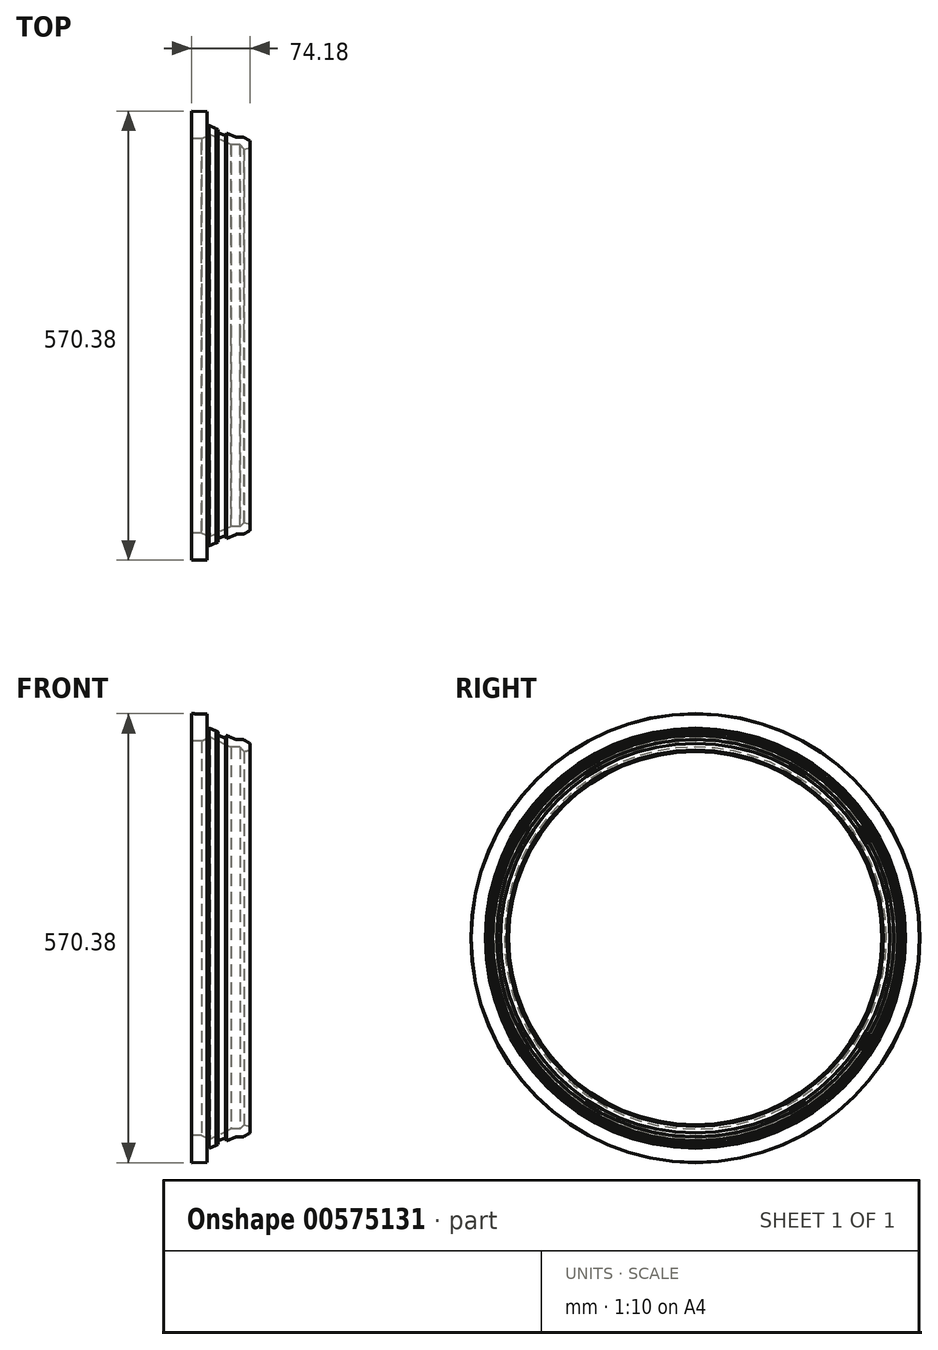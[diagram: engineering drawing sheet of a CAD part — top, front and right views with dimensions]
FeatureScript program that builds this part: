
annotation { "Feature Type Name" : "Feature", "Feature Type Description" : "" }
export const myFeature = defineFeature(function(context is Context, id is Id, definition is map)
    precondition{}
    {
        {
            var Q0;
            Q0=qCreatedBy(makeId("Front.planeOp"),FACE);
            var sketch = newSketch(context, id + "F0", { "sketchPlane" : qUnion([Q0])});
            skLineSegment(sketch, "E0", {"start": v(0, 0) * mm, "end": v(30.12, 0) * mm});
            skPoint(sketch, "E1", {"position": v(-7.36, 231.93) * mm});
            skLineSegment(sketch, "E2", {"start": v(-7.36, 237.1) * mm, "end": v(0, 239.08) * mm});
            skLineSegment(sketch, "E3.trimOffspring", {"start": v(0, 239.08) * mm, "end": v(0, 245.2) * mm});
            skLineSegment(sketch, "E4", {"start": v(-7.36, 237.1) * mm, "end": v(-12.82, 242.57) * mm});
            skLineSegment(sketch, "E5", {"start": v(-16.97, 252.22) * mm, "end": v(-8.98, 252.22) * mm});
            skLineSegment(sketch, "E6", {"start": v(-97.44, 148.32) * mm, "end": v(22.45, 148.32) * mm});
            skLineSegment(sketch, "E7", {"start": v(-97.44, 193.92) * mm, "end": v(-97.44, 70.08) * mm});
            skPoint(sketch, "E8", {"position": v(-66.59, 139.32) * mm});
            skArc(sketch, "E9", {"start": v(0, 247.47) * mm, "mid": v(-3.92, 249.79) * mm, "end": v(-7.93, 251.96) * mm});
            skLineSegment(sketch, "E10", {"start": v(0, 0) * mm, "end": v(0, 148.32) * mm});
            skArc(sketch, "E11.trimOffspring", {"start": v(-43.28, 263.2) * mm, "mid": v(-47.44, 265.06) * mm, "end": v(-51.66, 266.78) * mm});
            skLineSegment(sketch, "E12", {"start": v(-43.28, 263.2) * mm, "end": v(-40.28, 261.92) * mm});
            skLineSegment(sketch, "E13", {"start": v(-40.28, 261.92) * mm, "end": v(-41.77, 258.41) * mm});
            skLineSegment(sketch, "E14", {"start": v(-41.77, 258.41) * mm, "end": v(-31.25, 253.95) * mm});
            skLineSegment(sketch, "E15", {"start": v(-31.25, 253.95) * mm, "end": v(-29.76, 257.46) * mm});
            skLineSegment(sketch, "E16.trimOffspring", {"start": v(-29.76, 257.46) * mm, "end": v(-17.86, 252.4) * mm});
            skLineSegment(sketch, "E17.trimOffspring", {"start": v(0, 240.83) * mm, "end": v(0, 246.18) * mm});
            skLineSegment(sketch, "E18", {"start": v(-51.66, 266.78) * mm, "end": v(-52.3, 266.15) * mm});
            skLineSegment(sketch, "E19", {"start": v(-54.33, 266.06) * mm, "end": v(-52.5, 266.06) * mm});
            skLineSegment(sketch, "E20", {"start": v(-54.61, 284.8) * mm, "end": v(-54.61, 266.35) * mm});
            skLineSegment(sketch, "E21", {"start": v(-24.13, 242.57) * mm, "end": v(-13.94, 242.57) * mm});
            skPoint(sketch, "E22", {"position": v(-24.13, 242.57) * mm});
            skLineSegment(sketch, "E23", {"start": v(-13.94, 242.57) * mm, "end": v(-12.82, 242.57) * mm});
            skLineSegment(sketch, "E24", {"start": v(-24.13, 242.57) * mm, "end": v(-50.68, 255.32) * mm});
            skLineSegment(sketch, "E25", {"start": v(-50.68, 255.32) * mm, "end": v(-61.45, 250.42) * mm});
            skLineSegment(sketch, "E26", {"start": v(-61.45, 250.42) * mm, "end": v(-74.18, 250.42) * mm});
            skLineSegment(sketch, "E27", {"start": v(-74.18, 250.42) * mm, "end": v(-74.18, 285.19) * mm});
            skLineSegment(sketch, "E28", {"start": v(-74.18, 285.19) * mm, "end": v(-54.61, 284.8) * mm});
            skPoint(sketch, "E29.visualSharp", {"position": v(0, 247.47) * mm});
            skPoint(sketch, "E30.visualSharp", {"position": v(0, 239.08) * mm});
            skPoint(sketch, "E31.visualSharp", {"position": v(-8.43, 252.22) * mm});
            skArc(sketch, "E31.filletArc", {"start": v(-7.93, 251.96) * mm, "mid": v(-8.44, 252.16) * mm, "end": v(-8.98, 252.22) * mm});
            skPoint(sketch, "E32.visualSharp", {"position": v(-17.43, 252.22) * mm});
            skArc(sketch, "E32.filletArc", {"start": v(-17.86, 252.4) * mm, "mid": v(-17.42, 252.27) * mm, "end": v(-16.97, 252.22) * mm});
            skPoint(sketch, "E33.visualSharp", {"position": v(-51.66, 266.78) * mm});
            skPoint(sketch, "E34.visualSharp", {"position": v(-52.38, 266.06) * mm});
            skArc(sketch, "E34.filletArc", {"start": v(-52.5, 266.06) * mm, "mid": v(-52.4, 266.09) * mm, "end": v(-52.3, 266.15) * mm});
            skPoint(sketch, "E35.visualSharp", {"position": v(-54.61, 266.06) * mm});
            skArc(sketch, "E35.filletArc", {"start": v(-54.61, 266.35) * mm, "mid": v(-54.53, 266.15) * mm, "end": v(-54.33, 266.06) * mm});
            skPoint(sketch, "E36.visualSharp", {"position": v(-7.36, 237.1) * mm});
            skLineSegment(sketch, "E37", {"start": v(0, 246.18) * mm, "end": v(0, 247.47) * mm});
            skSolve(sketch);
        }
        {
            var Q0;
            Q0 = qSketchRegion(id + "F0", true);
            var Q1;
            Q1=sQuery(id+"F0.wireOp",EDGE,"E0");
            revolve(context, id + "F1", {"entities" : qUnion([Q0]), "axis" : qUnion([Q1]), "revolveType" : RevolveType.FULL});
        }
    });
